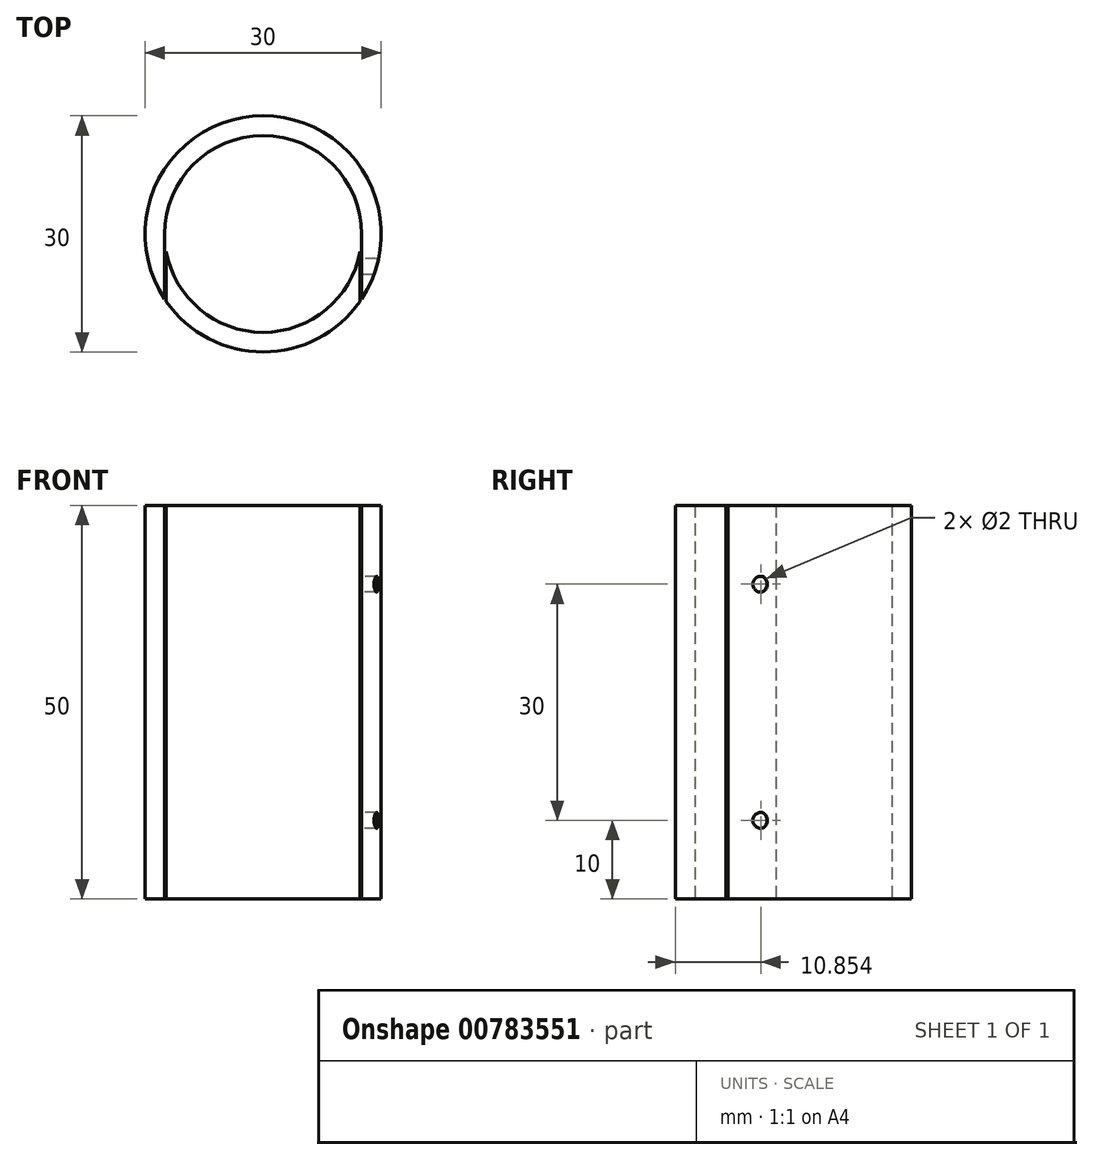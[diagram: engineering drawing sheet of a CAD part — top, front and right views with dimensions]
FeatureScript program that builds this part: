
annotation { "Feature Type Name" : "Feature", "Feature Type Description" : "" }
export const myFeature = defineFeature(function(context is Context, id is Id, definition is map)
    precondition{}
    {
        {
            var Q0;
            Q0=qCreatedBy(makeId("Top.planeOp"),FACE);
            var sketch = newSketch(context, id + "F0", { "sketchPlane" : qUnion([Q0])});
            skArc(sketch, "E0", {"start": v(12.5, -8.3) * mm, "mid": v(0, 15) * mm, "end": v(-12.5, -8.3) * mm});
            skArc(sketch, "E1", {"start": v(12.5, 0) * mm, "mid": v(0, 12.5) * mm, "end": v(-12.5, 0) * mm});
            skLineSegment(sketch, "E2", {"start": v(12.5, 0) * mm, "end": v(12.5, -8.3) * mm});
            skLineSegment(sketch, "E3", {"start": v(-12.5, 0) * mm, "end": v(-12.5, -8.3) * mm});
            skSolve(sketch);
        }
        {
            var Q0;
            Q0 = qSketchRegion(id + "F0", true);
            extrude(context, id + "F1", {"entities" : qUnion([Q0]), "depth" : 50 * mm, "offsetDistance" : 25 * mm});
        }
        {
            var Q0;
            Q0=qCreatedBy(makeId("Top.planeOp"),FACE);
            var sketch = newSketch(context, id + "F2", { "sketchPlane" : qUnion([Q0])});
            skArc(sketch, "E4", {"start": v(-12.3, -8.59) * mm, "mid": v(0, -15) * mm, "end": v(12.3, -8.59) * mm});
            skArc(sketch, "E5", {"start": v(-12.3, -2.23) * mm, "mid": v(0, -12.5) * mm, "end": v(12.3, -2.23) * mm});
            skLineSegment(sketch, "E6", {"start": v(12.3, -8.59) * mm, "end": v(12.3, -2.23) * mm});
            skLineSegment(sketch, "E7", {"start": v(-12.3, -8.59) * mm, "end": v(-12.3, -2.23) * mm});
            skSolve(sketch);
        }
        {
            var Q0;
            Q0 = qSketchRegion(id + "F2", true);
            extrude(context, id + "F3", {"entities" : qUnion([Q0]), "depth" : 50 * mm, "offsetDistance" : 25 * mm});
        }
        {
            var Q0;
            Q0=makeQuery(id+"F1.opExtrude","SWEPT_FACE",FACE,{"disambiguationData":[OSD([sQuery(id+"F0.wireOp",EDGE,"E2")])]});
            var sketch = newSketch(context, id + "F4", { "sketchPlane" : qUnion([Q0])});
            skLineSegment(sketch, "E8", {"start": v(4.15, 50) * mm, "end": v(4.15, 0) * mm, "construction": true});
            skPoint(sketch, "E9", {"position": v(4.15, 40) * mm});
            skPoint(sketch, "E10", {"position": v(4.15, 10) * mm});
            skSolve(sketch);
        }
        {
            var Q0;
            Q0=sQuery(id+"F4.wireOp",VERTEX,"E9");
            var Q1;
            Q1=sQuery(id+"F4.wireOp",VERTEX,"E10");
            var Q2;
            Q2=makeQuery(id+"F1.opExtrude","SWEPT_BODY",BODY,{"disambiguationData":[OSD([sQuery(id+"F0.wireOp",EDGE,"E0"),sQuery(id+"F0.wireOp",EDGE,"E1"),sQuery(id+"F0.wireOp",EDGE,"E2"),sQuery(id+"F0.wireOp",EDGE,"E3")])]});
            hole(context, id + "F5", {"style" : HoleStyle.SIMPLE, "endStyle" : HoleEndStyle.BLIND, "holeDiameter" : 2 * mm, "majorDiameter" : 5 * mm, "holeDepth" : 2 * mm, "isTappedThrough" : true, "tappedDepth" : 12 * mm, "tapClearance" : 3, "startFromSketch" : true, "locations" : qUnion([Q0, Q1]), "scope" : qUnion([Q2])});
        }
    });
